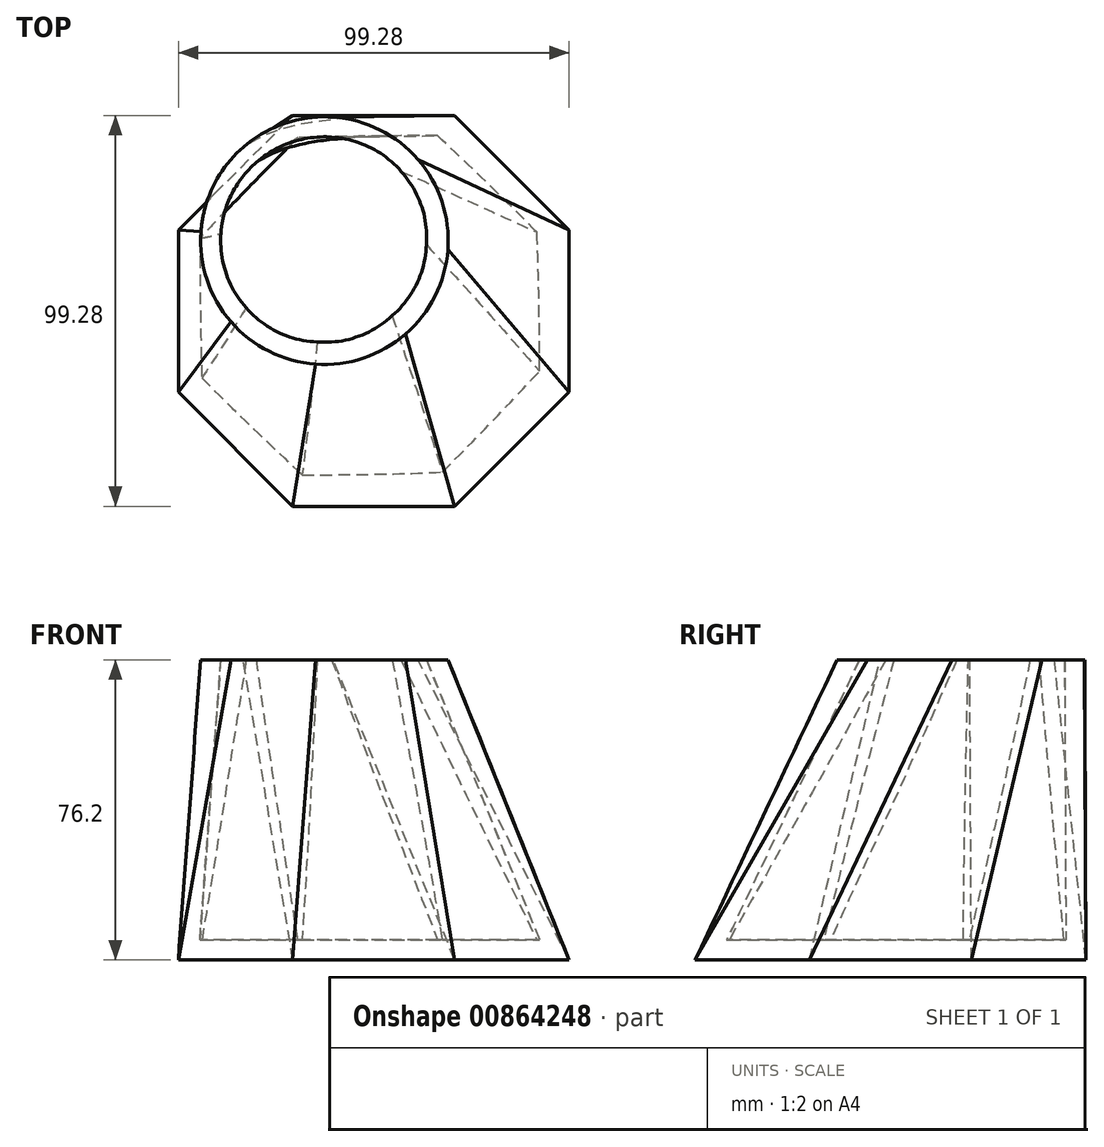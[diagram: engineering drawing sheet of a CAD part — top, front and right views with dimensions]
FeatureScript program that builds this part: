
annotation { "Feature Type Name" : "Feature", "Feature Type Description" : "" }
export const myFeature = defineFeature(function(context is Context, id is Id, definition is map)
    precondition{}
    {
        {
            var Q0;
            Q0=qCreatedBy(makeId("Top.planeOp"),FACE);
            var sketch = newSketch(context, id + "F0", { "sketchPlane" : qUnion([Q0])});
            skCircle(sketch, "E0.cCircle", {"center": v(0, 0) * mm, "radius": 49.64 * mm, "construction": true});
            skLineSegment(sketch, "E0.0", {"start": v(-49.64, 20.56) * mm, "end": v(-20.56, 49.64) * mm});
            skLineSegment(sketch, "E0.1", {"start": v(-20.56, 49.64) * mm, "end": v(20.56, 49.64) * mm});
            skLineSegment(sketch, "E0.2", {"start": v(20.56, 49.64) * mm, "end": v(49.64, 20.56) * mm});
            skLineSegment(sketch, "E0.3", {"start": v(49.64, 20.56) * mm, "end": v(49.64, -20.56) * mm});
            skLineSegment(sketch, "E0.4", {"start": v(49.64, -20.56) * mm, "end": v(20.56, -49.64) * mm});
            skLineSegment(sketch, "E0.5", {"start": v(20.56, -49.64) * mm, "end": v(-20.56, -49.64) * mm});
            skLineSegment(sketch, "E0.6", {"start": v(-20.56, -49.64) * mm, "end": v(-49.64, -20.56) * mm});
            skLineSegment(sketch, "E0.7", {"start": v(-49.64, -20.56) * mm, "end": v(-49.64, 20.56) * mm});
            skPoint(sketch, "E0.0.midPoint", {"position": v(-35.1, 35.1) * mm});
            skSolve(sketch);
        }
        {
            var Q0;
            Q0=qCreatedBy(makeId("Top.planeOp"),FACE);
            cPlane(context, id + "F1", {"entities" : qUnion([Q0]), "cplaneType" : CPlaneType.OFFSET, "offset" : 76.2 * mm, "width" : 152.4 * mm, "height" : 152.4 * mm});
        }
        {
            var Q0;
            Q0=qCreatedBy(id+"F1.planeOp",FACE);
            var sketch = newSketch(context, id + "F2", { "sketchPlane" : qUnion([Q0])});
            skCircle(sketch, "E1", {"center": v(-12.53, 17.9) * mm, "radius": 31.45 * mm});
            skSolve(sketch);
        }
        {
            var Q0;
            Q0=makeQuery(id+"F0.imprint","IMPRINT",FACE,{"disambiguationData":[TD([[makeQuery(id+"F0.imprint","IMPRINT",EDGE,{"derivedFrom":sQuery(id+"F0.wireOp",EDGE,"E0.0")}),-1.0]])]});
            var Q1;
            Q1=makeQuery(id+"F2.imprint","IMPRINT",FACE,{"disambiguationData":[TD([[makeQuery(id+"F2.imprint","IMPRINT",EDGE,{"derivedFrom":sQuery(id+"F2.wireOp",EDGE,"E1")}),1.0]])]});
            loft(context, id + "F3", {"sheetProfilesArray" : [{ "sheetProfileEntities" : qUnion([Q0]) }, { "sheetProfileEntities" : qUnion([Q1]) }]});
        }
        {
            var Q0;
            Q0=makeQuery(id+"F3.opLoft","CAP_FACE",FACE,{"disambiguationData":[OSD([makeQuery(id+"F2.imprint","IMPRINT",FACE,{"disambiguationData":[TD([[makeQuery(id+"F2.imprint","IMPRINT",EDGE,{"derivedFrom":sQuery(id+"F2.wireOp",EDGE,"E1")}),1.0]])]})])],"isStart":true});
            shell(context, id + "F4", {"entities" : qUnion([Q0]), "thickness" : 5.08 * mm});
        }
    });
